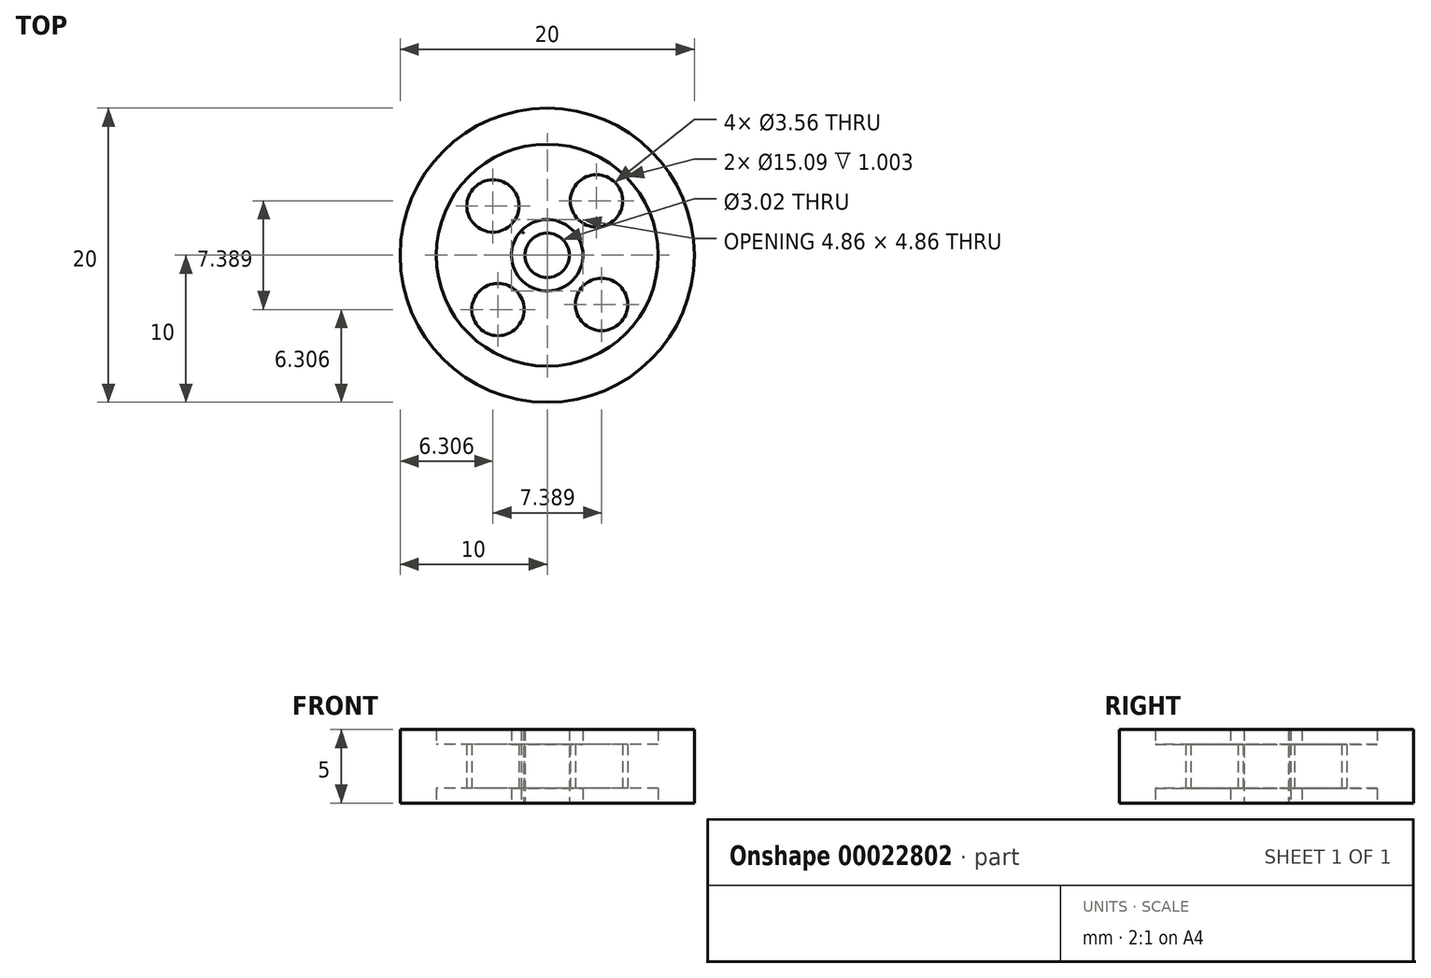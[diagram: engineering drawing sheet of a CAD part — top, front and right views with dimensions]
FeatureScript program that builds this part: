
annotation { "Feature Type Name" : "Feature", "Feature Type Description" : "" }
export const myFeature = defineFeature(function(context is Context, id is Id, definition is map)
    precondition{}
    {
        {
            var Q0;
            Q0=qCreatedBy(makeId("Top.planeOp"),FACE);
            var sketch = newSketch(context, id + "F0", { "sketchPlane" : qUnion([Q0])});
            skCircle(sketch, "E0", {"center": v(0, 0) * mm, "radius": 10 * mm});
            skCircle(sketch, "E1", {"center": v(0, 0) * mm, "radius": 7.55 * mm});
            skPoint(sketch, "E2.orphan", {"position": v(-6.93, 2.98) * mm});
            skCircle(sketch, "E3", {"center": v(0, 0) * mm, "radius": 2.43 * mm});
            skCircle(sketch, "E4", {"center": v(0, 0) * mm, "radius": 1.51 * mm});
            skPoint(sketch, "E5.center.orphan", {"position": v(-3.47, 1.5) * mm});
            skLineSegment(sketch, "E6.trimOffspring", {"start": v(-1.51, 0) * mm, "end": v(1.51, 0) * mm});
            skPoint(sketch, "E7.start.orphan", {"position": v(-10, 0) * mm});
            skLineSegment(sketch, "E8", {"start": v(0, 0) * mm, "end": v(0, 1.51) * mm});
            skPoint(sketch, "E9.center", {"position": v(0.14, -0.14) * mm});
            skLineSegment(sketch, "E10", {"start": v(0, 0) * mm, "end": v(-1.1, 1.04) * mm});
            skArc(sketch, "E11.trimOffspring", {"start": v(-1.78, 1.66) * mm, "mid": v(-1.7, 1.59) * mm, "end": v(-1.6, 1.52) * mm});
            skPoint(sketch, "E12.trimOffspring.end.orphan", {"position": v(0, 7.55) * mm});
            skLineSegment(sketch, "E13", {"start": v(1.7, 1.73) * mm, "end": v(5, 5.66) * mm});
            skCircle(sketch, "E14", {"center": v(3.35, 3.7) * mm, "radius": 1.78 * mm});
            skCircle(sketch, "E15.1.0", {"center": v(-3.7, 3.35) * mm, "radius": 1.78 * mm});
            skCircle(sketch, "E15.2.0", {"center": v(-3.35, -3.7) * mm, "radius": 1.78 * mm});
            skCircle(sketch, "E15.3.0", {"center": v(3.7, -3.35) * mm, "radius": 1.78 * mm});
            skLineSegment(sketch, "E16.trimOffspring", {"start": v(-1.6, 1.52) * mm, "end": v(-2.33, 2.21) * mm});
            skSolve(sketch);
        }
        {
            var Q0;
            Q0=makeQuery(id+"F0.imprint","IMPRINT",FACE,{"disambiguationData":[TD([[makeQuery(id+"F0.imprint","IMPRINT",EDGE,{"derivedFrom":sQuery(id+"F0.wireOp",EDGE,"E0")}),1.0]])]});
            extrude(context, id + "F1", {"entities" : qUnion([Q0]), "endBound" : BoundingType.SYMMETRIC, "depth" : 5 * mm});
        }
        {
            var Q0;
            Q0=makeQuery(id+"F0.imprint","IMPRINT",FACE,{"disambiguationData":[TD([[makeQuery(id+"F0.imprint","IMPRINT",EDGE,{"derivedFrom":sQuery(id+"F0.wireOp",EDGE,"E1")}),1.0]])]});
            extrude(context, id + "F2", {"entities" : qUnion([Q0]), "operationType" : NewBodyOperationType.ADD, "endBound" : BoundingType.SYMMETRIC, "depth" : 3 * mm});
        }
        {
            var Q0;
            {var subQ3=sQuery(id+"F0.wireOp",EDGE,"E11.trimOffspring");Q0=makeQuery(id+"F0.imprint","IMPRINT",FACE,{"disambiguationData":[TD([[makeQuery(id+"F0.imprint","IMPRINT",EDGE,{"derivedFrom":subQ3}),-1.0]])]});}
            extrude(context, id + "F3", {"entities" : qUnion([Q0]), "operationType" : NewBodyOperationType.ADD, "endBound" : BoundingType.SYMMETRIC, "depth" : 5 * mm});
        }
    });
